SOLIDWORKS PART (.sldprt)
format: sldprt  version: not decoded by parser v0  size: 150,528 bytes
history: native  units: mm
features: sketch x3, extrude x3, material x1 (+16 scaffold rows collapsed)
feature tree (23):
  scaffold x16  (default folders/planes/origin — collapsed)
  material  "Material <not specified>"
  sketch  "Sketch1"  dims[D1=100.0mm]
  extrude  "Extrude1"  Depth=28490mm
  sketch  "Sketch2"  dims[c1.D1=3500.0mm c1.D2=~3841.830094mm c2.D1=6000.0mm c2.D2=~4475.912204mm c3.D1=~20317.742298mm c3.D2=6000.0mm c3.D3=~6773.92832mm]
  extrude  "Extrude2"  Depth=100mm
  sketch  "Sketch3"  dims[D1=0.0mm]
  extrude  "Extrude3"  Depth=100mm
decode coverage: 6 of 6 modeling features carry decoded parameters
note: ~ marks probable driven/reference dimensions
note: suppression state not decoded; provenance and decode notes live in map.json
